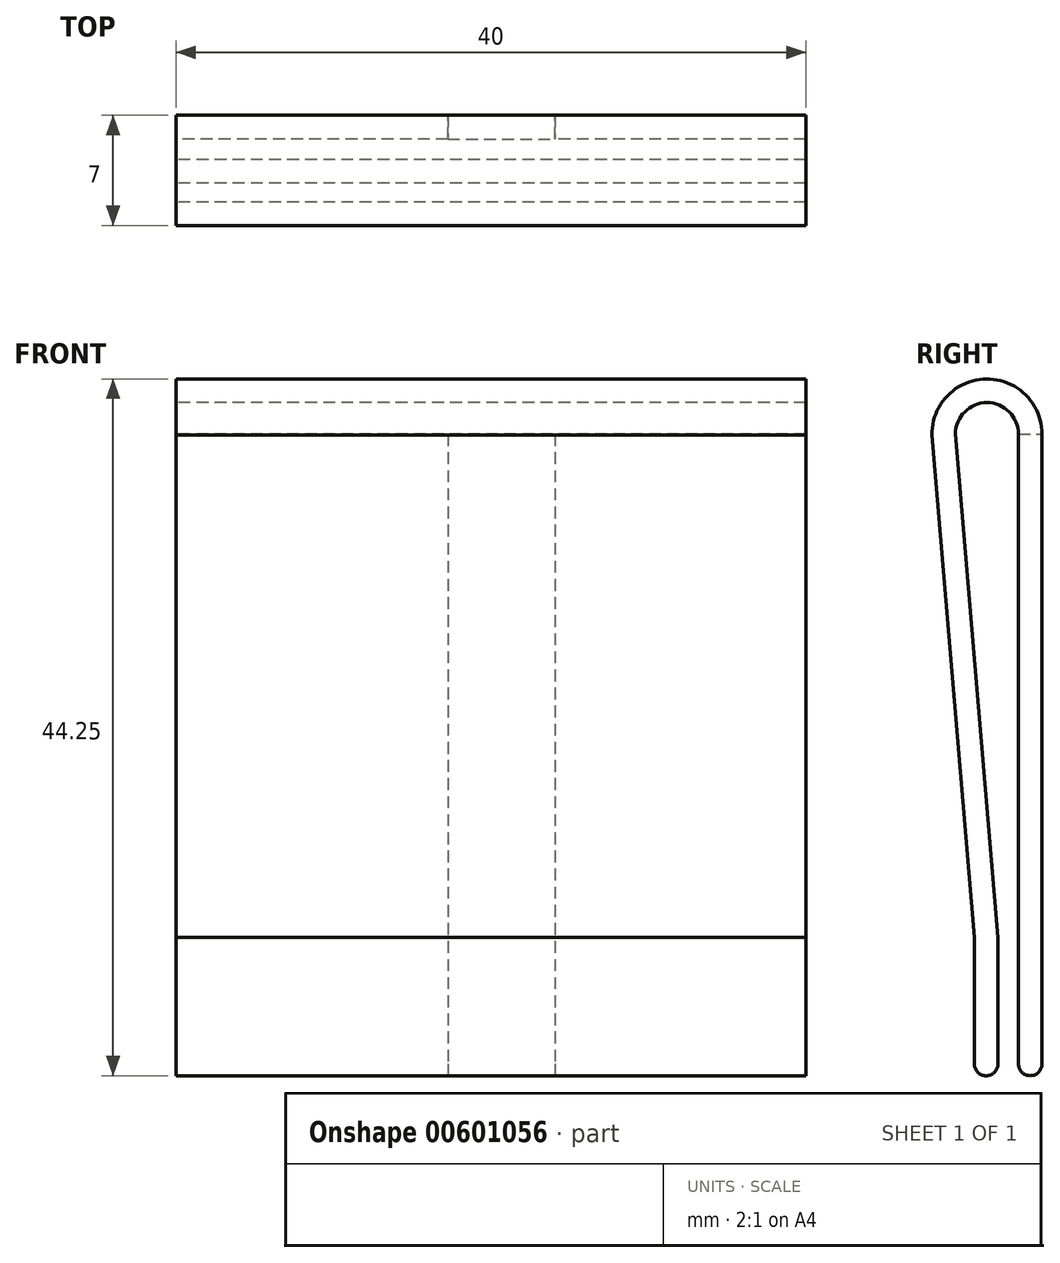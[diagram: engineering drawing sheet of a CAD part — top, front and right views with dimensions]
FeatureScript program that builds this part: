
annotation { "Feature Type Name" : "Feature", "Feature Type Description" : "" }
export const myFeature = defineFeature(function(context is Context, id is Id, definition is map)
    precondition{}
    {
        {
            var Q0;
            Q0=qCreatedBy(makeId("Right.planeOp"),FACE);
            var sketch = newSketch(context, id + "F0", { "sketchPlane" : qUnion([Q0])});
            skLineSegment(sketch, "E0", {"start": v(-38.53, -18.01) * mm, "end": v(-38.53, 21.99) * mm});
            skLineSegment(sketch, "E1", {"start": v(-42.53, 21.99) * mm, "end": v(-39.83, -9.98) * mm});
            skArc(sketch, "E2", {"start": v(-38.53, 21.99) * mm, "mid": v(-40.53, 23.99) * mm, "end": v(-42.53, 21.99) * mm});
            skArc(sketch, "E3.0", {"start": v(-37.03, 21.99) * mm, "mid": v(-40.57, 25.49) * mm, "end": v(-44.03, 21.92) * mm});
            skLineSegment(sketch, "E4", {"start": v(-44.03, 21.92) * mm, "end": v(-41.34, -9.98) * mm});
            skLineSegment(sketch, "E5", {"start": v(-39.83, -9.98) * mm, "end": v(-39.83, -18.01) * mm});
            skLineSegment(sketch, "E6", {"start": v(-41.34, -9.98) * mm, "end": v(-41.34, -18.01) * mm});
            skArc(sketch, "E7", {"start": v(-41.34, -18.01) * mm, "mid": v(-40.58, -18.76) * mm, "end": v(-39.83, -18.01) * mm});
            skLineSegment(sketch, "E8", {"start": v(-37.03, 21.99) * mm, "end": v(-37.03, -18.01) * mm});
            skArc(sketch, "E9", {"start": v(-38.53, -18.01) * mm, "mid": v(-37.78, -18.76) * mm, "end": v(-37.03, -18.01) * mm});
            skSolve(sketch);
        }
        {
            var Q0;
            Q0 = qSketchRegion(id + "F0", true);
            extrude(context, id + "F1", {"entities" : qUnion([Q0]), "depth" : 40 * mm, "offsetDistance" : 25 * mm});
        }
        {
            var Q0;
            Q0=qCreatedBy(makeId("Front.planeOp"),FACE);
            var sketch = newSketch(context, id + "F2", { "sketchPlane" : qUnion([Q0])});
            skLineSegment(sketch, "E10.bottom", {"start": v(24.06, 21.99) * mm, "end": v(17.26, 21.99) * mm});
            skLineSegment(sketch, "E10.top", {"start": v(17.26, -28.81) * mm, "end": v(24.06, -28.81) * mm});
            skLineSegment(sketch, "E10.left", {"start": v(17.26, -28.81) * mm, "end": v(17.26, 21.99) * mm});
            skLineSegment(sketch, "E10.right", {"start": v(24.06, -28.81) * mm, "end": v(24.06, 21.99) * mm});
            skSolve(sketch);
        }
        {
            var Q0;
            Q0 = qSketchRegion(id + "F2", true);
            extrude(context, id + "F3", {"entities" : qUnion([Q0]), "operationType" : NewBodyOperationType.REMOVE, "depth" : 39.5 * mm, "offsetDistance" : 25 * mm});
        }
    });
